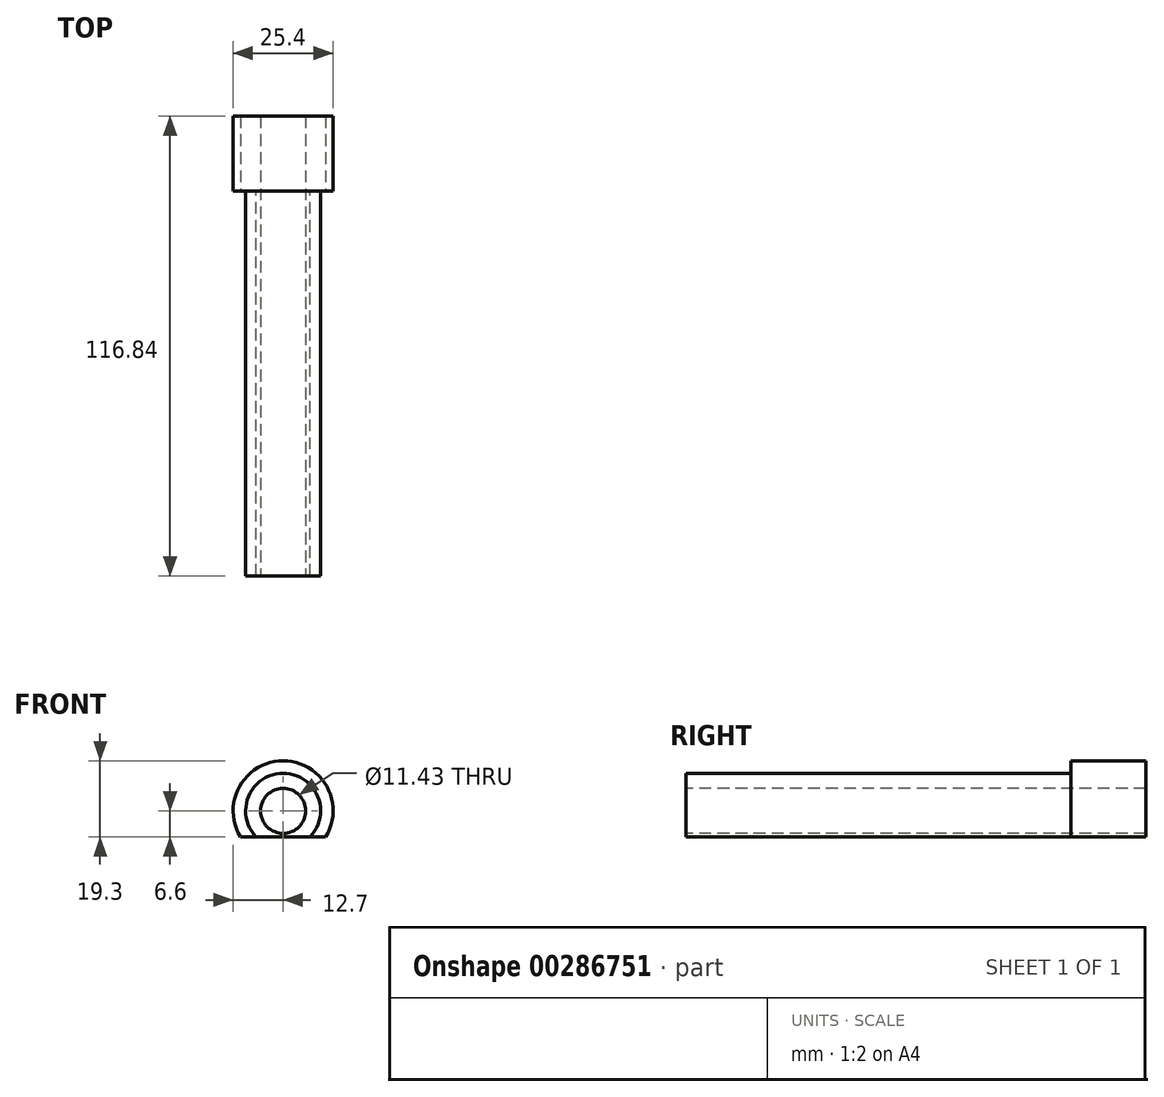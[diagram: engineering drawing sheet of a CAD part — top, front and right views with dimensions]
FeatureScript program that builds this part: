
annotation { "Feature Type Name" : "Feature", "Feature Type Description" : "" }
export const myFeature = defineFeature(function(context is Context, id is Id, definition is map)
    precondition{}
    {
        {
            var Q0;
            Q0=qCreatedBy(makeId("Front.planeOp"),FACE);
            var sketch = newSketch(context, id + "F0", { "sketchPlane" : qUnion([Q0])});
            skCircle(sketch, "E0", {"center": v(0, 0) * mm, "radius": 5.72 * mm});
            skArc(sketch, "E1", {"start": v(10.85, -6.6) * mm, "mid": v(0, 12.7) * mm, "end": v(-10.85, -6.6) * mm});
            skLineSegment(sketch, "E2", {"start": v(-10.85, -6.6) * mm, "end": v(10.85, -6.6) * mm});
            skSolve(sketch);
        }
        {
            var Q0;
            Q0=makeQuery(id+"F0.imprint","IMPRINT",FACE,{"disambiguationData":[TD([[makeQuery(id+"F0.imprint","IMPRINT",EDGE,{"derivedFrom":sQuery(id+"F0.wireOp",EDGE,"E0")}),-1.0]])]});
            extrude(context, id + "F1", {"entities" : qUnion([Q0]), "oppositeDirection" : true, "depth" : 19.05 * mm});
        }
        {
            var Q0;
            Q0=qCreatedBy(makeId("Front.planeOp"),FACE);
            var sketch = newSketch(context, id + "F2", { "sketchPlane" : qUnion([Q0])});
            skCircle(sketch, "E3", {"center": v(0, 0) * mm, "radius": 5.72 * mm});
            skArc(sketch, "E4", {"start": v(6.86, -6.6) * mm, "mid": v(0, 9.53) * mm, "end": v(-6.86, -6.6) * mm});
            skLineSegment(sketch, "E5", {"start": v(-6.86, -6.6) * mm, "end": v(6.86, -6.6) * mm});
            skSolve(sketch);
        }
        {
            var Q0;
            Q0=makeQuery(id+"F2.imprint","IMPRINT",FACE,{"disambiguationData":[TD([[makeQuery(id+"F2.imprint","IMPRINT",EDGE,{"derivedFrom":sQuery(id+"F2.wireOp",EDGE,"E3")}),-1.0]])]});
            extrude(context, id + "F3", {"entities" : qUnion([Q0]), "operationType" : NewBodyOperationType.ADD, "depth" : 97.8 * mm});
        }
    });
